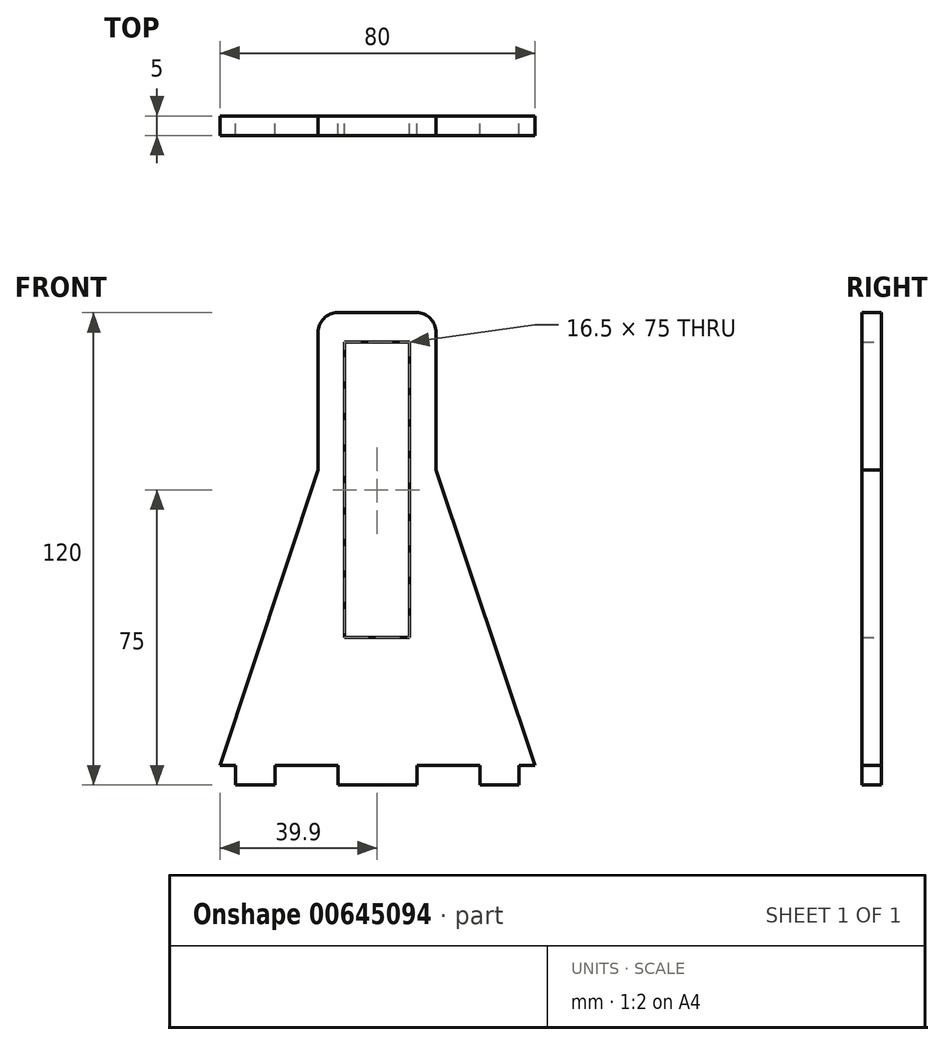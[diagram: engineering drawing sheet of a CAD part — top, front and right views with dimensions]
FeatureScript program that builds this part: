
annotation { "Feature Type Name" : "Feature", "Feature Type Description" : "" }
export const myFeature = defineFeature(function(context is Context, id is Id, definition is map)
    precondition{}
    {
        {
            var Q0;
            Q0=qCreatedBy(makeId("Front.planeOp"),FACE);
            var sketch = newSketch(context, id + "F0", { "sketchPlane" : qUnion([Q0])});
            skLineSegment(sketch, "E0.bottom", {"start": v(15, -20) * mm, "end": v(-15, -20) * mm});
            skLineSegment(sketch, "E0.top", {"start": v(15, 20) * mm, "end": v(-15, 20) * mm});
            skLineSegment(sketch, "E0.left", {"start": v(15, -20) * mm, "end": v(15, 20) * mm});
            skLineSegment(sketch, "E0.right", {"start": v(-15, -20) * mm, "end": v(-15, 20) * mm});
            skPoint(sketch, "E0.middle", {"position": v(0, 0) * mm});
            skLineSegment(sketch, "E1", {"start": v(-35.9, -95) * mm, "end": v(-35.9, -100) * mm});
            skLineSegment(sketch, "E2", {"start": v(-35.9, -100) * mm, "end": v(-25.9, -100) * mm});
            skLineSegment(sketch, "E3", {"start": v(-25.9, -100) * mm, "end": v(-25.9, -95) * mm});
            skLineSegment(sketch, "E4", {"start": v(26.1, -95) * mm, "end": v(26.1, -100) * mm});
            skLineSegment(sketch, "E5", {"start": v(26.1, -100) * mm, "end": v(36.1, -100) * mm});
            skLineSegment(sketch, "E6", {"start": v(36.1, -100) * mm, "end": v(36.1, -95) * mm});
            skLineSegment(sketch, "E7.left", {"start": v(-9.9, -100) * mm, "end": v(-9.9, -95) * mm});
            skLineSegment(sketch, "E7.right", {"start": v(10.1, -100) * mm, "end": v(10.1, -95) * mm});
            skLineSegment(sketch, "E8", {"start": v(-9.9, -95) * mm, "end": v(-25.9, -95) * mm});
            skLineSegment(sketch, "E9", {"start": v(10.1, -95) * mm, "end": v(26.1, -95) * mm});
            skLineSegment(sketch, "E10", {"start": v(-9.9, -100) * mm, "end": v(10.1, -100) * mm});
            skLineSegment(sketch, "E11", {"start": v(-35.9, -95) * mm, "end": v(-39.9, -95) * mm});
            skLineSegment(sketch, "E12", {"start": v(36.1, -95) * mm, "end": v(40.1, -95) * mm});
            skLineSegment(sketch, "E13", {"start": v(-39.9, -95) * mm, "end": v(-15, -20) * mm});
            skLineSegment(sketch, "E14", {"start": v(40.1, -95) * mm, "end": v(15, -20) * mm});
            skLineSegment(sketch, "E15.bottom", {"start": v(8.25, -12.5) * mm, "end": v(-8.25, -12.5) * mm});
            skLineSegment(sketch, "E15.top", {"start": v(8.25, 12.5) * mm, "end": v(-8.25, 12.5) * mm});
            skLineSegment(sketch, "E15.left", {"start": v(8.25, -12.5) * mm, "end": v(8.25, 12.5) * mm});
            skLineSegment(sketch, "E15.right", {"start": v(-8.25, -12.5) * mm, "end": v(-8.25, 12.5) * mm});
            skLineSegment(sketch, "E16.bottom", {"start": v(-8.25, -12.5) * mm, "end": v(8.25, -12.5) * mm});
            skLineSegment(sketch, "E16.top", {"start": v(-8.25, -62.5) * mm, "end": v(8.25, -62.5) * mm});
            skLineSegment(sketch, "E16.left", {"start": v(-8.25, -12.5) * mm, "end": v(-8.25, -62.5) * mm});
            skLineSegment(sketch, "E16.right", {"start": v(8.25, -12.5) * mm, "end": v(8.25, -62.5) * mm});
            skSolve(sketch);
        }
        {
            var Q0;
            Q0 = qSketchRegion(id + "F0", true);
            extrude(context, id + "F1", {"entities" : qUnion([Q0]), "depth" : 5 * mm, "offsetDistance" : 25 * mm});
        }
        {
            var Q0;
            Q0=makeQuery(id+"F1.opExtrude","SWEPT_EDGE",EDGE,{"disambiguationData":[OSD([sQuery(id+"F0.wireOp",EDGE,"E0.top"),sQuery(id+"F0.wireOp",EDGE,"E0.right")])]});
            fillet(context, id + "F2", {"entities" : qUnion([Q0]), "radius" : 5 * mm, "tangentPropagation" : true, "allowEdgeOverflow" : false});
        }
        {
            var Q0;
            Q0=makeQuery(id+"F1.opExtrude","SWEPT_EDGE",EDGE,{"disambiguationData":[OSD([sQuery(id+"F0.wireOp",EDGE,"E0.top"),sQuery(id+"F0.wireOp",EDGE,"E0.left")])]});
            fillet(context, id + "F3", {"entities" : qUnion([Q0]), "radius" : 5 * mm, "tangentPropagation" : true, "allowEdgeOverflow" : false});
        }
    });
